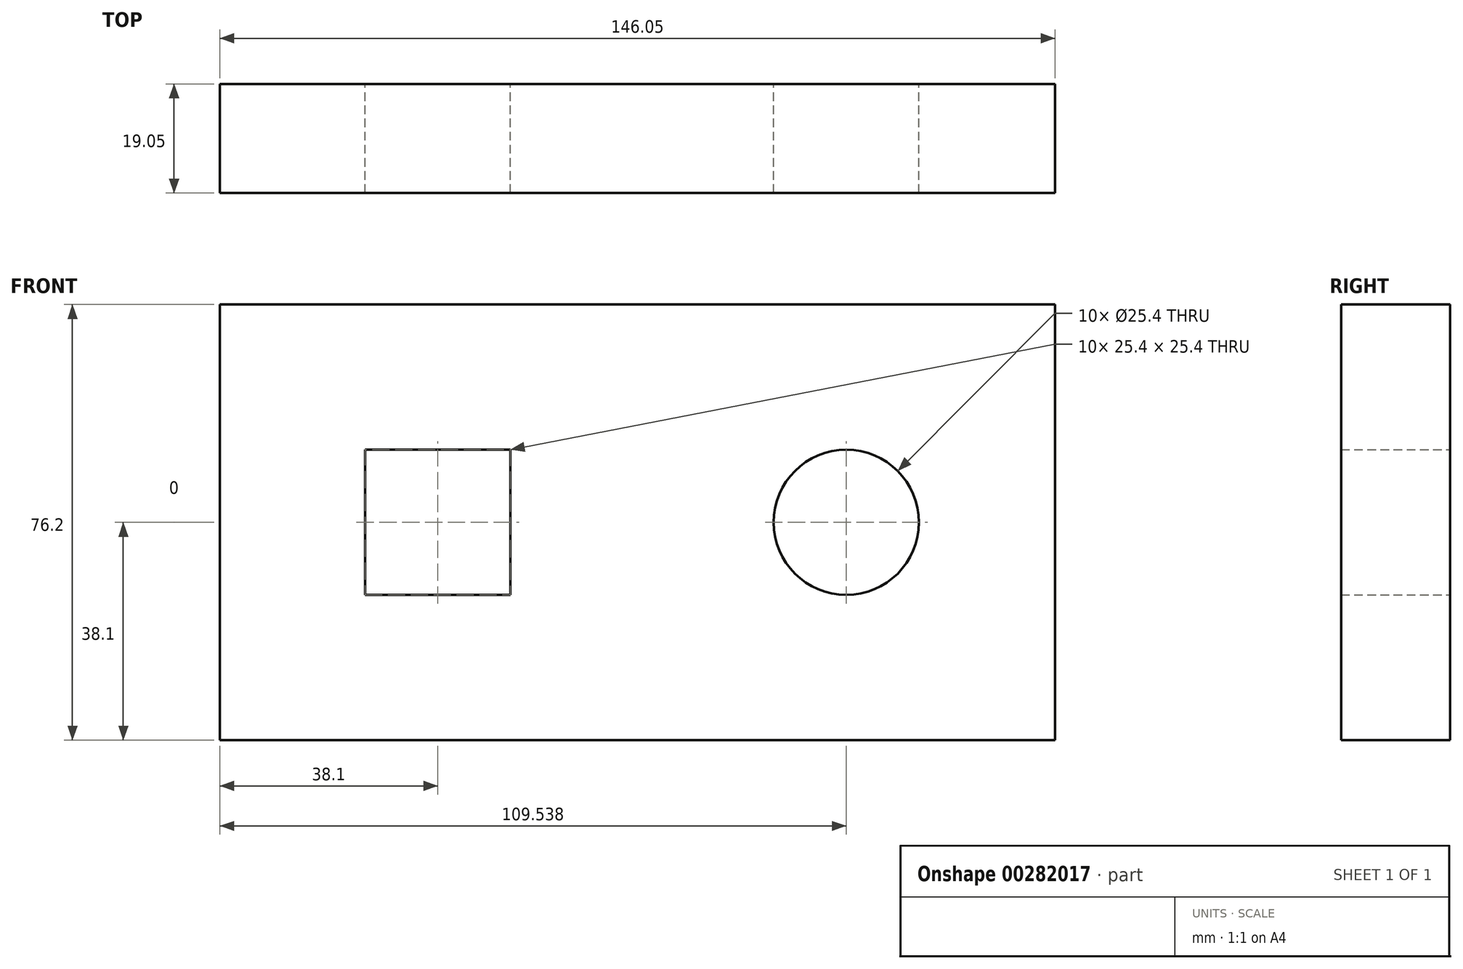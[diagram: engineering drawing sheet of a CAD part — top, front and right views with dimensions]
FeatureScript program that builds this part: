
annotation { "Feature Type Name" : "Feature", "Feature Type Description" : "" }
export const myFeature = defineFeature(function(context is Context, id is Id, definition is map)
    precondition{}
    {
        {
            var Q0;
            Q0=qCreatedBy(makeId("Front.planeOp"),FACE);
            var sketch = newSketch(context, id + "F0", { "sketchPlane" : qUnion([Q0])});
            skLineSegment(sketch, "E0.bottom", {"start": v(0, 0) * mm, "end": v(-146.05, 0) * mm});
            skLineSegment(sketch, "E0.top", {"start": v(0, 76.2) * mm, "end": v(-146.05, 76.2) * mm});
            skLineSegment(sketch, "E0.left", {"start": v(0, 0) * mm, "end": v(0, 76.2) * mm});
            skLineSegment(sketch, "E0.right", {"start": v(-146.05, 0) * mm, "end": v(-146.05, 76.2) * mm});
            skLineSegment(sketch, "E1.bottom", {"start": v(-120.65, 50.8) * mm, "end": v(-95.25, 50.8) * mm});
            skLineSegment(sketch, "E1.top", {"start": v(-120.65, 25.4) * mm, "end": v(-95.25, 25.4) * mm});
            skLineSegment(sketch, "E1.left", {"start": v(-120.65, 50.8) * mm, "end": v(-120.65, 25.4) * mm});
            skLineSegment(sketch, "E1.right", {"start": v(-95.25, 50.8) * mm, "end": v(-95.25, 25.4) * mm});
            skCircle(sketch, "E2", {"center": v(-36.51, 38.1) * mm, "radius": 12.7 * mm});
            skSolve(sketch);
        }
        {
            var Q0;
            Q0 = qSketchRegion(id + "F0", true);
            extrude(context, id + "F1", {"entities" : qUnion([Q0]), "depth" : 19.05 * mm});
        }
    });
